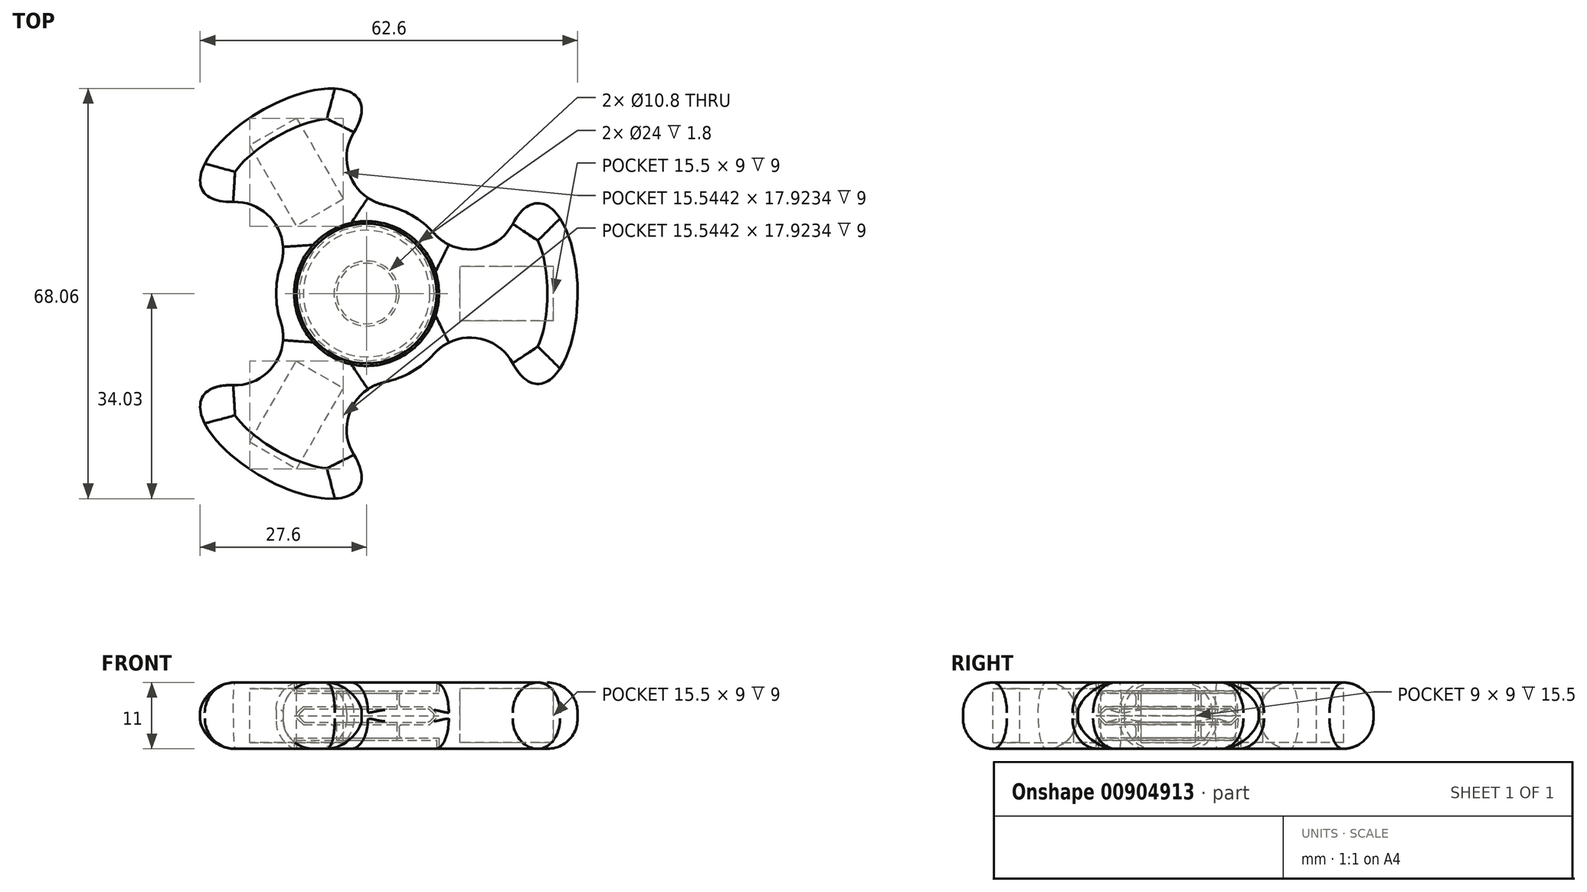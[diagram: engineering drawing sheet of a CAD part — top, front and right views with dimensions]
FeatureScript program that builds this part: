
annotation { "Feature Type Name" : "Feature", "Feature Type Description" : "" }
export const myFeature = defineFeature(function(context is Context, id is Id, definition is map)
    precondition{}
    {
        {
            var Q0;
            Q0=qCreatedBy(makeId("Front.planeOp"),FACE);
            var sketch = newSketch(context, id + "F0", { "sketchPlane" : qUnion([Q0])});
            skLineSegment(sketch, "E0", {"start": v(0, 0) * mm, "end": v(0, 5.5) * mm});
            skLineSegment(sketch, "E1", {"start": v(0, 5.5) * mm, "end": v(11.6, 5.5) * mm});
            skLineSegment(sketch, "E2", {"start": v(5, 1.1) * mm, "end": v(10.33, 1.1) * mm});
            skLineSegment(sketch, "E3", {"start": v(10.33, 1.1) * mm, "end": v(11.43, 0) * mm});
            skLineSegment(sketch, "E4", {"start": v(5, 1.1) * mm, "end": v(5, 4.1) * mm});
            skLineSegment(sketch, "E5", {"start": v(5, 4.1) * mm, "end": v(11.6, 4.1) * mm});
            skLineSegment(sketch, "E6", {"start": v(11.6, 4.1) * mm, "end": v(11.6, 5.5) * mm});
            skLineSegment(sketch, "E7", {"start": v(0, 0) * mm, "end": v(11.43, 0) * mm, "construction": true});
            skLineSegment(sketch, "E8.MirrorCS", {"start": v(0, 0) * mm, "end": v(0, -5.5) * mm});
            skLineSegment(sketch, "E9.MirrorCS", {"start": v(0, -5.5) * mm, "end": v(11.6, -5.5) * mm});
            skLineSegment(sketch, "E10.MirrorCS", {"start": v(11.6, -4.1) * mm, "end": v(11.6, -5.5) * mm});
            skLineSegment(sketch, "E11.MirrorCS", {"start": v(5, -4.1) * mm, "end": v(11.6, -4.1) * mm});
            skLineSegment(sketch, "E12.MirrorCS", {"start": v(5, -1.1) * mm, "end": v(5, -4.1) * mm});
            skLineSegment(sketch, "E13.MirrorCS", {"start": v(5, -1.1) * mm, "end": v(10.33, -1.1) * mm});
            skLineSegment(sketch, "E14.MirrorCS", {"start": v(10.33, -1.1) * mm, "end": v(11.43, 0) * mm});
            skLineSegment(sketch, "E15.0", {"start": v(12, 3.7) * mm, "end": v(12, 5.5) * mm});
            skLineSegment(sketch, "E15.1", {"start": v(5.4, 3.7) * mm, "end": v(12, 3.7) * mm});
            skLineSegment(sketch, "E15.2", {"start": v(5.4, 1.5) * mm, "end": v(5.4, 3.7) * mm});
            skLineSegment(sketch, "E15.3", {"start": v(5.4, 1.5) * mm, "end": v(10.5, 1.5) * mm});
            skLineSegment(sketch, "E15.4", {"start": v(10.5, 1.5) * mm, "end": v(12, 0) * mm});
            skLineSegment(sketch, "E15.5", {"start": v(10.5, -1.5) * mm, "end": v(12, 0) * mm});
            skLineSegment(sketch, "E15.6", {"start": v(12, -3.7) * mm, "end": v(12, -5.5) * mm});
            skLineSegment(sketch, "E15.7", {"start": v(5.4, -3.7) * mm, "end": v(12, -3.7) * mm});
            skLineSegment(sketch, "E15.8", {"start": v(5.4, -1.5) * mm, "end": v(5.4, -3.7) * mm});
            skLineSegment(sketch, "E15.9", {"start": v(5.4, -1.5) * mm, "end": v(10.5, -1.5) * mm});
            skLineSegment(sketch, "E16", {"start": v(12, 5.5) * mm, "end": v(15, 5.5) * mm});
            skLineSegment(sketch, "E17", {"start": v(15, 5.5) * mm, "end": v(15, -5.5) * mm});
            skLineSegment(sketch, "E18", {"start": v(15, -5.5) * mm, "end": v(12, -5.5) * mm});
            skSolve(sketch);
        }
        {
            var Q0;
            Q0=makeQuery(id+"F0.imprint","IMPRINT",FACE,{"disambiguationData":[TD([[makeQuery(id+"F0.imprint","IMPRINT",EDGE,{"derivedFrom":sQuery(id+"F0.wireOp",EDGE,"E0")}),-1.0]])]});
            var Q1;
            Q1=makeQuery(id+"F0.imprint","IMPRINT",FACE,{"disambiguationData":[TD([[makeQuery(id+"F0.imprint","IMPRINT",EDGE,{"derivedFrom":sQuery(id+"F0.wireOp",EDGE,"E15.0")}),-1.0]])]});
            var Q2;
            Q2=sQuery(id+"F0.wireOp",EDGE,"E0");
            revolve(context, id + "F1", {"surfaceOperationType" : NewSurfaceOperationType.NEW, "entities" : qUnion([Q0, Q1]), "axis" : qUnion([Q2]), "revolveType" : RevolveType.FULL});
        }
        {
            var Q0;
            Q0=makeQuery(id+"F1.opRevolve","SWEPT_EDGE",EDGE,{"disambiguationData":[OSD([sQuery(id+"F0.wireOp",EDGE,"E2"),sQuery(id+"F0.wireOp",EDGE,"E3")])]});
            var Q1;
            Q1=makeQuery(id+"F1.opRevolve","SWEPT_EDGE",EDGE,{"disambiguationData":[OSD([sQuery(id+"F0.wireOp",EDGE,"E3"),sQuery(id+"F0.wireOp",EDGE,"E14.MirrorCS")])]});
            var Q2;
            Q2=makeQuery(id+"F1.opRevolve","SWEPT_EDGE",EDGE,{"disambiguationData":[OSD([sQuery(id+"F0.wireOp",EDGE,"E13.MirrorCS"),sQuery(id+"F0.wireOp",EDGE,"E14.MirrorCS")])]});
            var Q3;
            Q3=makeQuery(id+"F1.opRevolve","SWEPT_EDGE",EDGE,{"disambiguationData":[OSD([sQuery(id+"F0.wireOp",EDGE,"E15.1"),sQuery(id+"F0.wireOp",EDGE,"E15.2")])]});
            var Q4;
            Q4=makeQuery(id+"F1.opRevolve","SWEPT_EDGE",EDGE,{"disambiguationData":[OSD([sQuery(id+"F0.wireOp",EDGE,"E15.8"),sQuery(id+"F0.wireOp",EDGE,"E15.9")])]});
            var Q5;
            Q5=makeQuery(id+"F1.opRevolve","SWEPT_EDGE",EDGE,{"disambiguationData":[OSD([sQuery(id+"F0.wireOp",EDGE,"E15.7"),sQuery(id+"F0.wireOp",EDGE,"E15.8")])]});
            var Q6;
            Q6=makeQuery(id+"F1.opRevolve","SWEPT_EDGE",EDGE,{"disambiguationData":[OSD([sQuery(id+"F0.wireOp",EDGE,"E15.2"),sQuery(id+"F0.wireOp",EDGE,"E15.3")])]});
            fillet(context, id + "F2", {"entities" : qUnion([Q0, Q1, Q2, Q3, Q4, Q5, Q6]), "radius" : .5 * mm, "tangentPropagation" : true, "allowEdgeOverflow" : false});
        }
        {
            var Q0;
            Q0=makeQuery(id+"F1.opRevolve","SWEPT_FACE",FACE,{"disambiguationData":[OSD([sQuery(id+"F0.wireOp",EDGE,"E18")])]});
            var sketch = newSketch(context, id + "F3", { "sketchPlane" : qUnion([Q0])});
            skCircle(sketch, "E19.0", {"center": v(0, 0) * mm, "radius": 15 * mm});
            skArc(sketch, "E20", {"start": v(24.23, -11.56) * mm, "mid": v(18.12, -7.37) * mm, "end": v(11.2, -9.99) * mm});
            skArc(sketch, "E21", {"start": v(11.2, 9.99) * mm, "mid": v(18.12, 7.37) * mm, "end": v(24.23, 11.56) * mm});
            skCircle(sketch, "E22", {"center": v(0, 0) * mm, "radius": 35 * mm, "construction": true});
            skEllipse(sketch, "E23", {"center": v(28.42, 0) * mm, "majorRadius": 15 * mm, "minorRadius": 6.58 * mm, "majorAxis": v(0, 1)});
            skSolve(sketch);
        }
        {
            var Q0;
            {var subQ1=sQuery(id+"F3.wireOp",EDGE,"E20");Q0=makeQuery(id+"F3.imprint","IMPRINT",FACE,{"disambiguationData":[TD([[makeQuery(id+"F3.imprint","IMPRINT",EDGE,{"derivedFrom":subQ1}),-1.0]])]});}
            var Q1;
            {var subQ0=sQuery(id+"F3.wireOp",EDGE,"C8lxOGX4-ROlp-XFIU-pVnN-gfc84VBz0n8b");var subQ1=makeQuery(id+"F3.imprint","INTERSECT",VERTEX,{"derivedFrom":[sQuery(id+"F3.wireOp",EDGE,"E20"),subQ0]});Q1=makeQuery(id+"F3.imprint","IMPRINT",FACE,{"disambiguationData":[TD([[makeQuery(id+"F3.imprint","IMPRINT",EDGE,{"disambiguationData":[TD([[subQ1,1.0]])],"derivedFrom":subQ0}),1.0]])]});}
            var Q2;
            {var subQ0=sQuery(id+"F3.wireOp",EDGE,"E23");var subQ1=makeQuery(id+"F3.imprint","INTERSECT",VERTEX,{"derivedFrom":[sQuery(id+"F3.wireOp",EDGE,"E20"),subQ0]});Q2=makeQuery(id+"F3.imprint","IMPRINT",FACE,{"disambiguationData":[TD([[makeQuery(id+"F3.imprint","IMPRINT",EDGE,{"disambiguationData":[TD([[subQ1,1.0]])],"derivedFrom":subQ0}),1.0]])]});}
            var Q3;
            Q3=makeQuery(id+"F1.opRevolve","SWEPT_FACE",FACE,{"disambiguationData":[OSD([sQuery(id+"F0.wireOp",EDGE,"E16")])]});
            extrude(context, id + "F4", {"entities" : qUnion([Q0, Q1, Q2]), "endBound" : BoundingType.UP_TO_SURFACE, "oppositeDirection" : true, "depth" : 25 * mm, "endBoundEntityFace" : qUnion([Q3]), "offsetDistance" : 25 * mm});
        }
        {
            var Q0;
            Q0=makeQuery(id+"F4.opExtrude","CAP_FACE",FACE,{"disambiguationData":[OSD([sQuery(id+"F3.wireOp",EDGE,"E19.0"),sQuery(id+"F3.wireOp",EDGE,"E20"),sQuery(id+"F3.wireOp",EDGE,"E21"),sQuery(id+"F3.wireOp",EDGE,"E23")])],"isStart":false});
            var sketch = newSketch(context, id + "F5", { "sketchPlane" : qUnion([Q0])});
            skLineSegment(sketch, "E24.bottom", {"start": v(31, -4.5) * mm, "end": v(15.5, -4.5) * mm});
            skLineSegment(sketch, "E24.top", {"start": v(31, 4.5) * mm, "end": v(15.5, 4.5) * mm});
            skLineSegment(sketch, "E24.left", {"start": v(31, -4.5) * mm, "end": v(31, 4.5) * mm});
            skLineSegment(sketch, "E24.right", {"start": v(15.5, -4.5) * mm, "end": v(15.5, 4.5) * mm});
            skPoint(sketch, "E24.middle", {"position": v(23.25, 0) * mm});
            skSolve(sketch);
        }
        {
            var Q0;
            Q0=makeQuery(id+"F5.imprint","IMPRINT",FACE,{"disambiguationData":[TD([[makeQuery(id+"F5.imprint","IMPRINT",EDGE,{"derivedFrom":sQuery(id+"F5.wireOp",EDGE,"E24.bottom")}),-1.0]])]});
            extrude(context, id + "F6", {"entities" : qUnion([Q0]), "operationType" : NewBodyOperationType.REMOVE, "oppositeDirection" : true, "depth" : 10 * mm, "offsetDistance" : 25 * mm});
        }
        {
            var Q0;
            Q0=makeQuery(id+"F5.imprint","IMPRINT",FACE,{"disambiguationData":[TD([[makeQuery(id+"F5.imprint","IMPRINT",EDGE,{"derivedFrom":sQuery(id+"F5.wireOp",EDGE,"E24.bottom")}),-1.0]])]});
            extrude(context, id + "F7", {"entities" : qUnion([Q0]), "operationType" : NewBodyOperationType.ADD, "oppositeDirection" : true, "depth" : 1 * mm, "offsetDistance" : 25 * mm});
        }
        {
            var Q0;
            Q0=makeQuery(id+"F4.opExtrude","SWEPT_BODY",BODY,{"disambiguationData":[OSD([sQuery(id+"F3.wireOp",EDGE,"E19.0"),sQuery(id+"F3.wireOp",EDGE,"E20"),sQuery(id+"F3.wireOp",EDGE,"E21"),sQuery(id+"F3.wireOp",EDGE,"E23")])]});
            var Q1;
            Q1=sQuery(id+"F0.wireOp",EDGE,"E0");
            circularPattern(context, id + "F8", {"operationType" : NewBodyOperationType.ADD, "entities" : qUnion([Q0]), "axis" : qUnion([Q1]), "angle" : 360 * degree, "instanceCount" : 3, "equalSpace" : true});
        }
        {
            var Q0;
            Q0=makeQuery(id+"F4.opExtrude","CAP_EDGE",EDGE,{"disambiguationData":[OSD([sQuery(id+"F3.wireOp",EDGE,"E23")])],"isStart":true});
            var Q1;
            Q1=makeQuery(id+"F4.opExtrude","CAP_EDGE",EDGE,{"disambiguationData":[OSD([sQuery(id+"F3.wireOp",EDGE,"E23")])],"isStart":false});
            fillet(context, id + "F9", {"entities" : qUnion([Q0, Q1]), "radius" : 5 * mm, "tangentPropagation" : true, "allowEdgeOverflow" : false});
        }
    });
